# Revit family: ElectricalFixture_WiringAccessories_Hager_Sollysta_ShaverSocket
name_source: partatom
category: Electrical Fixtures
revit_build: Autodesk Revit 2015 (Build: 20160512_1515(x64)
units: mm (PartAtom-declared; Revit-internal decimal feet)

## types (3) — shared parameters
CE Approval = Yes
Colour = SollystaWhite
Default Elevation = 1219.2 mm  [stored 4 ft]
Design Country = China
Distance From Centre = 22.4 mm
Distance From Edge = 63.6 mm
Expected Life = 25 years
Extrusion From Wall = 12.6 mm
Finish = Gloss
Frequency = 50/60Hz
Gross Weight kg = 0.165
LED Indicator Switch = Yes
Manufacturer = Hager
Manufacturer Country = United Kingdom
Manufacturer Website = http://www.hager.co.uk
Material = Urea Formaldehyde Thermoset Plastic
Overall Depth = 26.1 mm
Overall Height = 146 mm  [stored 0.479003 ft]
Overall Length = 65 mm  [stored 0.213255 ft]
Overall Width = 86 mm  [stored 0.282152 ft]
Packaging Recyclable = Yes
Product Group = WiringAccessories
Product Literature = http://www.hager.co.uk
Product Range = Sollysta
Product URL = http://www.hager.co.uk
Reference Standard = BS 1363-2
Shape = Rectangular
Shipping Weight kg = 0.188
Supply Phase = 1
Switch = Yes
Type = ElectricalFixture
Voltage (Volts) = 230V/240V

## per-type parameters (varying)
| type | Description | EAN Code | Features | Name | Product Family | Product Model Number | Technical Description | Unique Reference |
| WMCC50 | 2GangDoublePoleSwitchedSocketDualEarth | 5015652261117 | 2GangDoublePoleSwitchedSocketDualEarth | WhiteMoldedSocket_WMSS82 | WhiteMoldedSockets | WMSS82 | 2GangDoublePoleSwitchedSocketDualEarth | WMSS82 |
| WMSO100 | 115/230VoltShaverOutlet | 5015652261728 | 115/230VoltShaverOutlet | WhiteMouldedSocket_WMSO100 | WhiteMouldedSockets_ShaverSocket | WMSO100 | 115/230VoltShaverOutlet | WMSO100 |
| WMCC50N | 2GangDoublePoleSwitchedSocketDualEarth | 5015652261117 | 2GangDoublePoleSwitchedSocketDualEarth | WhiteMoldedSocket_WMSS82 | WhiteMoldedSockets | WMSS82 | 2GangDoublePoleSwitchedSocketDualEarth | WMSS82 |

note: [stored X ft] marks values corroborated as IEEE doubles in the binary element streams (Revit-internal decimal feet)

## geometry (parser evidence)
native form markers: Blend x2, Sweep x4
no freeform markers — native parametric forms only
